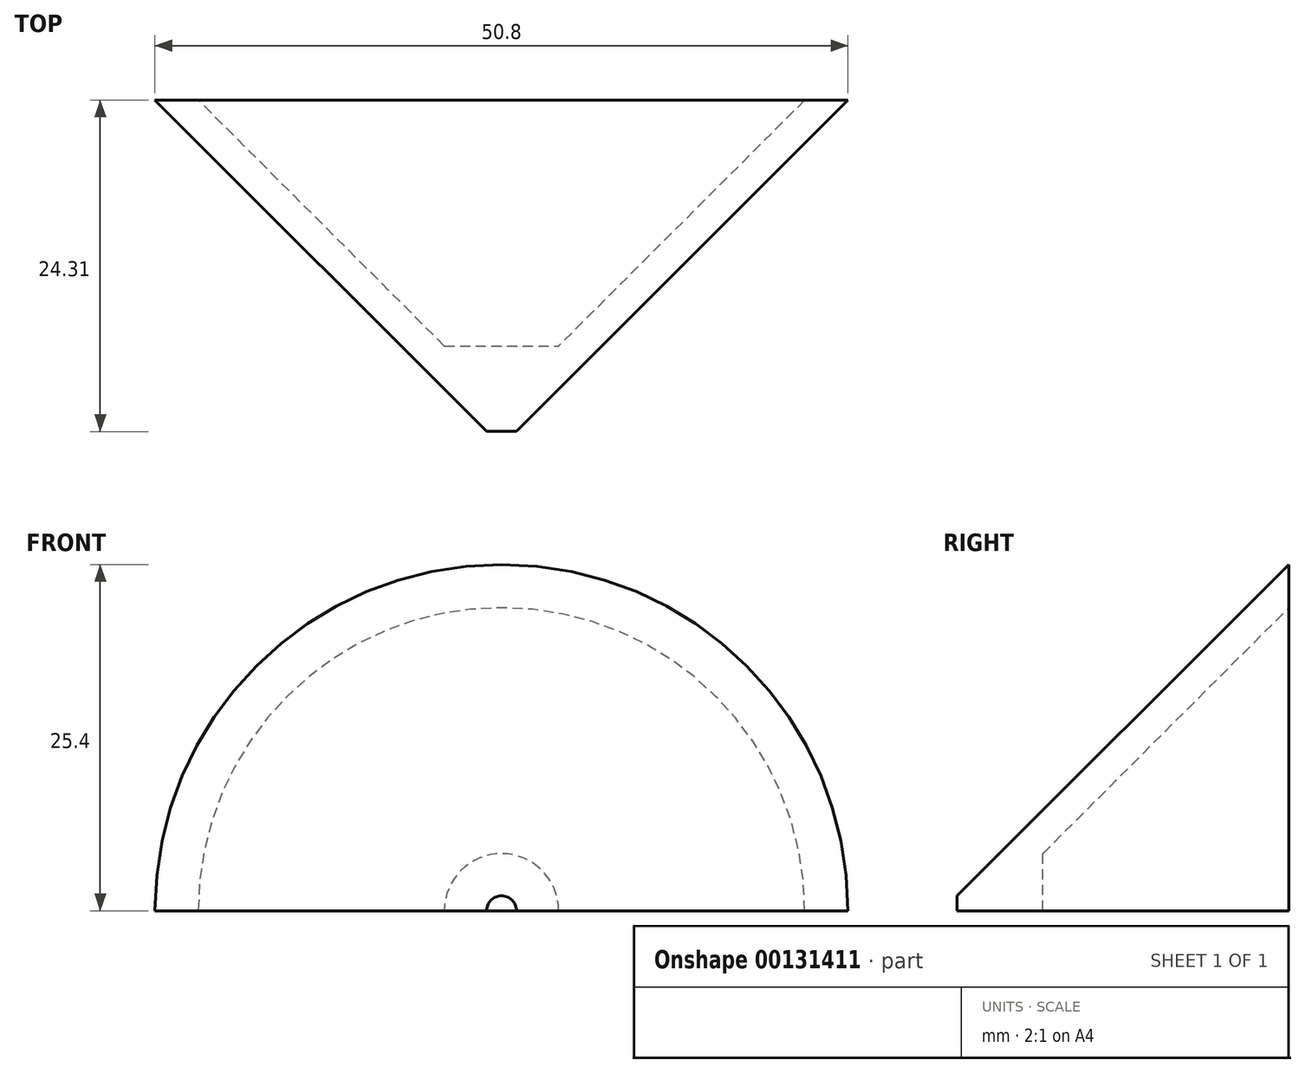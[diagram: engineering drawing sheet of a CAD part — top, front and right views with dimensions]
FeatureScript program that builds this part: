
annotation { "Feature Type Name" : "Feature", "Feature Type Description" : "" }
export const myFeature = defineFeature(function(context is Context, id is Id, definition is map)
    precondition{}
    {
        {
            var Q0;
            Q0=qCreatedBy(makeId("Front.planeOp"),FACE);
            var sketch = newSketch(context, id + "F0", { "sketchPlane" : qUnion([Q0])});
            skCircle(sketch, "E0", {"center": v(0, 0) * mm, "radius": 25.4 * mm});
            skSolve(sketch);
        }
        {
            var Q0;
            Q0=makeQuery(id+"F0.imprint","IMPRINT",FACE,{"disambiguationData":[TD([[makeQuery(id+"F0.imprint","IMPRINT",EDGE,{"derivedFrom":sQuery(id+"F0.wireOp",EDGE,"E0")}),1.0]])]});
            extrude(context, id + "F1", {"entities" : qUnion([Q0]), "depth" : 24.3 * mm, "hasDraft" : true, "draftAngle" : 45 * degree, "draftPullDirection" : true});
        }
        {
            var Q0;
            Q0=makeQuery(id+"F1.opExtrude","CAP_FACE",FACE,{"disambiguationData":[OSD([sQuery(id+"F0.wireOp",EDGE,"E0")])],"isStart":true});
            var sketch = newSketch(context, id + "F2", { "sketchPlane" : qUnion([Q0])});
            skCircle(sketch, "E1", {"center": v(0, 0) * mm, "radius": 22.23 * mm});
            skSolve(sketch);
        }
        {
            var Q0;
            Q0=makeQuery(id+"F1.opExtrude","CAP_FACE",FACE,{"disambiguationData":[OSD([sQuery(id+"F0.wireOp",EDGE,"E0")])],"isStart":true});
            var sketch = newSketch(context, id + "F3", { "sketchPlane" : qUnion([Q0])});
            skLineSegment(sketch, "E2.bottom", {"start": v(-25.4, 0) * mm, "end": v(25.4, 0) * mm});
            skLineSegment(sketch, "E2.top", {"start": v(-25.4, -26.16) * mm, "end": v(25.4, -26.16) * mm});
            skLineSegment(sketch, "E2.left", {"start": v(-25.4, 0) * mm, "end": v(-25.4, -26.16) * mm});
            skLineSegment(sketch, "E2.right", {"start": v(25.4, 0) * mm, "end": v(25.4, -26.16) * mm});
            skSolve(sketch);
        }
        {
            var Q0;
            Q0 = qSketchRegion(id + "F3", true);
            extrude(context, id + "F4", {"entities" : qUnion([Q0]), "operationType" : NewBodyOperationType.REMOVE, "oppositeDirection" : true, "depth" : 28.45 * mm});
        }
        {
            var Q0;
            Q0=makeQuery(id+"F2.imprint","IMPRINT",FACE,{"disambiguationData":[TD([[makeQuery(id+"F2.imprint","IMPRINT",EDGE,{"derivedFrom":sQuery(id+"F2.wireOp",EDGE,"E1")}),1.0]])]});
            extrude(context, id + "F5", {"entities" : qUnion([Q0]), "operationType" : NewBodyOperationType.REMOVE, "oppositeDirection" : true, "depth" : 18.03 * mm, "hasDraft" : true, "draftAngle" : 45 * degree, "draftPullDirection" : true});
        }
    });
